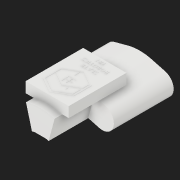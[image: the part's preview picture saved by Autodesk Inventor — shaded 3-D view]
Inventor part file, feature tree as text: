
AUTODESK INVENTOR PART (.ipt)
format: ipt  version: 2017 SP1 (Build 210196100, 196)  size: 504,832 bytes
history: native  units: in
note: dims shown in document units (in); Inventor stores cm internally (conversion verified against a paired STEP export)
features: extrude x5, sketch x5, plane x1
ambient origin geometry x8: Origin, YZ Plane, XZ Plane, XY Plane, X Axis, Y Axis, Z Axis, Center Point
bodies: Solid1 (feature_tree)
feature tree (11):
  extrude  "Extrusion1"  Depth=10.8268in TaperAngle=0.0deg
  extrude  "Extrusion2"  Depth=11.811in
  plane  "Work Plane1"
  extrude  "Extrusion3"  Depth=1.8701in
  extrude  "Extrusion4"  Depth=10.8268in
  extrude  "Extrusion5"  Depth=0.0787in TaperAngle=0.0deg
  sketch  "Sketch1"  dims[d0=6.2992in d1=3.937in d2=3.937in d3=6.2992in d4=6.2992in d5=6.2992in d6=75.0deg d7=75.0deg d8=6.2992in d9=3.937in d10=3.937in d11=0.4134in d12=0.4134in d13=4.4488in d14=8.3858in d15=0.7874in d16=12.4016in d17=0.4134in d18=0.597in d19=7.3031in d20=2.7559in d21=0.0in d22=10.8268in d23=0.0in]
  sketch  "Sketch2"  dims[d24=-6.1024in d25=11.811in]
  sketch  "Sketch3"  dims[d26=15.748in d27=1.8701in]
  sketch  "Sketch4"  dims[d28=2.8346in d29=0.0in]
  sketch  "Sketch5"  dims[d30=0.5906in d31=9.8425in d32=0.4016in d33=0.1673in d34=2.0669in d35=1.5748in d36=0.5512in d37=1.122in d38=0.5906in d39=0.9449in d40=1.8504in d41=0.9055in d42=2.0079in d43=2.0669in d44=0.9449in d45=0.9449in d46=0.9449in d47=0.9449in d48=0.9449in d49=0.9449in d50=0.9449in d51=0.9449in d54=11.811in d56=15.748in d94=0.0787in d95=0.0in d96=13.5827in d97=0.0in d98=0.7874in d99=0.7874in d100=10.8268in d101=0.0in]
